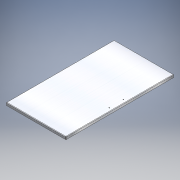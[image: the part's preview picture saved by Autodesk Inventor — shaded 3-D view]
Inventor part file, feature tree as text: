
AUTODESK INVENTOR PART (.ipt)
format: ipt  version: 2017 (Build 210142000, 142)  size: 379,392 bytes
history: native  units: mm
features: sheet_metal_op x8, sketch x8, other x5, hole x1, plane x1, chamfer x1
ambient origin geometry x8: Origin, YZ Plane, XZ Plane, XY Plane, X Axis, Y Axis, Z Axis, Center Point
bodies: Solid1 (feature_tree)
feature tree (24):
  sheet_metal_op  "Face1"
  sheet_metal_op  "Flange1"
  hole  "Hole1"  [1 undecoded]
  sheet_metal_op  "Hem1"
  sheet_metal_op  "Hem2"
  sheet_metal_op  "Hem3"
  sheet_metal_op  "Hem4"
  plane  "Work Plane1"
  other  "Decal1"
  chamfer  "Chamfer1"  Distance=1.5mm Angle=90.0deg
  sketch  "Sketch1"  dims[d6=1.5mm d7=1.5mm]
  other  "Plate1"
  sketch  "Sketch2"  dims[d8=0.75mm]
  other  "Plate2"
  sheet_metal_op  "Bend1"
  sheet_metal_op  "Corner1"
  sketch  "Sketch4"  dims[d9=3.0mm]
  sketch  "Sketch9"  dims[d24=25.0mm d26=100.0mm d27=4.5mm d28=6.0mm d29=4.0mm d30=2.0mm d31=90.0deg d32=1.5mm d33=20.594885mm d35=1.5mm d36=0.75mm d37=3.0mm d38=1.5mm d39=10.0mm d40=0.15mm d41=0.075mm d42=1.5mm d43=0.75mm d44=3.0mm d45=1.5mm d46=10.0mm d47=0.15mm d48=0.075mm d49=1.5mm d50=0.75mm d51=3.0mm d52=1.5mm d53=416.0mm d54=10.0mm d55=0.15mm d56=0.075mm d57=1.5mm d58=0.75mm d59=3.0mm d60=1.5mm d61=416.0mm d62=10.0mm d63=0.15mm d64=0.075mm d65=200.0mm d71=1.5mm d72=2.0mm d73=45.0deg d74=423.299mm d75=766.0mm d76=766.0mm d77=423.299mm d88=50.0mm]
  other  "Image1"
  sketch  "Sketch5"  dims[d10=1.5mm d11=20.0mm d12=90.0deg d13=1.5mm]
  sketch  "Sketch6"  dims[d14=6.0mm]
  sketch  "Sketch7"  dims[d15=1.5mm]
  sketch  "Sketch8"  dims[d16=1.5mm]
  other  "Definition1"
note: 1 required parameter value undecoded (feature->parameter linkage not recoverable at this tier; creation-order binding heuristic only, values carry confidence <= 0.55)
